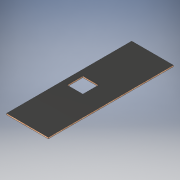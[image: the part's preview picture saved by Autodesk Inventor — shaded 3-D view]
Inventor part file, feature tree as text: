
AUTODESK INVENTOR PART (.ipt)
format: ipt  version: 2017 (Build 210142000, 142)  size: 102,400 bytes
history: native  units: in
note: dims shown in document units (in); Inventor stores cm internally (conversion verified against a paired STEP export)
features: extrude x1, sketch x1
ambient origin geometry x8: Origin, YZ Plane, XZ Plane, XY Plane, X Axis, Y Axis, Z Axis, Center Point
bodies: Solid1 (feature_tree)
feature tree (2):
  extrude  "Extrusion1"  Depth=16.0in
  sketch  "Sketch1"  dims[d0=48.0in d1=16.0in d2=4.0in d3=3.25in d4=3.5in d5=6.0in d6=6.0in d7=0.5in d8=0.0in]
